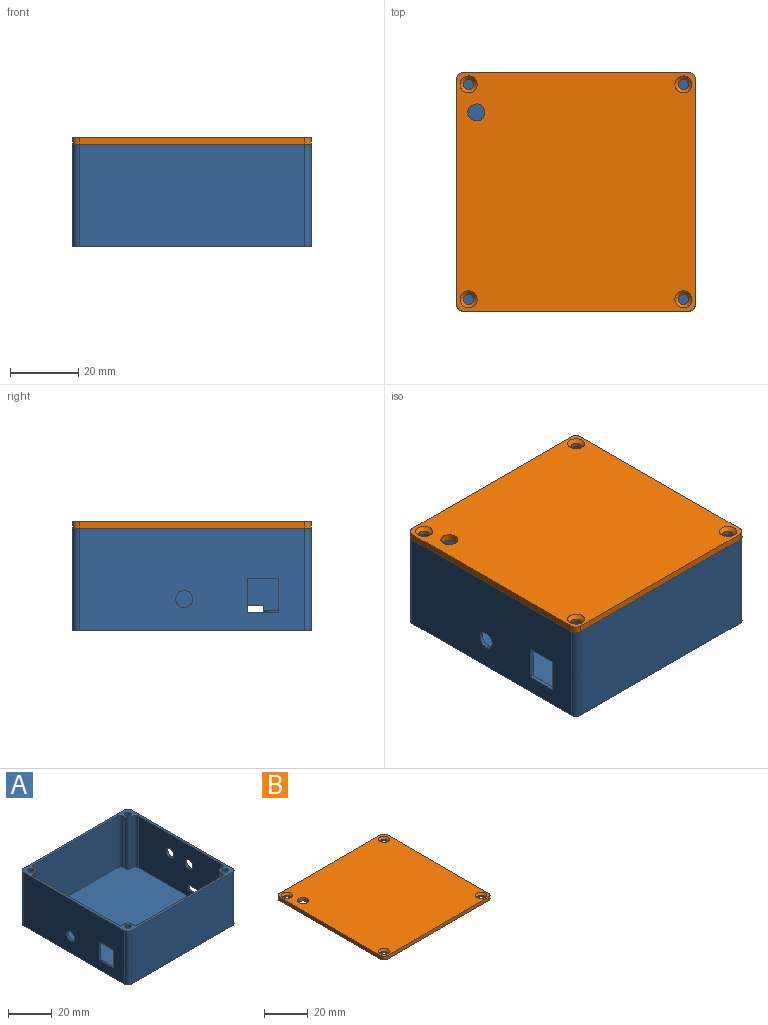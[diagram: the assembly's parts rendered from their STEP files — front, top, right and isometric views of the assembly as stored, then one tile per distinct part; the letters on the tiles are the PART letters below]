
ASSEMBLY  parts=2 mates=1
PART A: 60 faces, bbox 70x70x30 mm
  f0: plane 54x29mm, normal (1,0,0), area 1454.2mm2, adj f4,f7,f43,f48,f55,f56,f57,f58
  f1: plane 66x30mm, normal (-1,0,0), area 1868.2mm2, adj f7,f10,f27,f28,f55,f56,f57,f58
  f2: plane 54x29mm, normal (-1,0,0), area 1478.7mm2, adj f4,f7,f39,f42,f49,f50,f51,f52
  f3: plane 66x30mm, normal (1,0,0), area 1892.7mm2, adj f7,f10,f29,f30,f49,f50,f51,f52
  f4: plane 68x68mm, normal (0,0,1), area 4481.3mm2, adj f0,f2,f5,f6,f11,f12,f13,f14
  f5: plane 54x29mm, normal (0,1,0), area 1566mm2, adj f4,f7,f40,f44
  f6: plane 54x29mm, normal (0,-1,0), area 1566mm2, adj f4,f7,f38,f46
  f7: plane 70x70mm, normal (0,0,1), area 347.7mm2, adj f0,f1,f2,f3,f5,f6,f8,f9
  f8: plane 66x30mm, normal (0,1,0), area 1980mm2, adj f7,f10,f27,f30
  f9: plane 66x30mm, normal (0,-1,0), area 1980mm2, adj f7,f10,f28,f29
  f10: plane 70x70mm, normal (0,0,-1), area 4882.4mm2, adj f1,f3,f8,f9,f27,f28,f29,f30
  f11: plane 29x1mm, normal (0,-1,0), area 29mm2, adj f4,f7,f47,f48
  f12: plane 29x1mm, normal (1,0,0), area 29mm2, adj f4,f7,f46,f47
  f13: plane 29x1mm, normal (0,-1,0), area 29mm2, adj f4,f7,f37,f39
  f14: plane 29x1mm, normal (-1,0,0), area 29mm2, adj f4,f7,f37,f38
  f15: plane 29x1mm, normal (0,1,0), area 29mm2, adj f4,f7,f43,f45
  f16: plane 29x1mm, normal (1,0,0), area 29mm2, adj f4,f7,f44,f45
  f17: plane 29x1mm, normal (0,1,0), area 29mm2, adj f4,f7,f41,f42
  f18: plane 29x1mm, normal (-1,0,0), area 29mm2, adj f4,f7,f40,f41
  f19: cylinder r=1.5mm len=10mm, axis (0,0,1), area 94.2mm2, adj f7,f20
  f20: plane 3x3mm, normal (0,0,1), area 7.1mm2, adj f19
  f21: cylinder r=1.5mm len=10mm, axis (0,0,1), area 94.2mm2, adj f7,f22
  f22: plane 3x3mm, normal (0,0,1), area 7.1mm2, adj f21
  f23: cylinder r=1.5mm len=10mm, axis (0,0,1), area 94.2mm2, adj f7,f24
  f24: plane 3x3mm, normal (0,0,1), area 7.1mm2, adj f23
  f25: cylinder r=1.5mm len=10mm, axis (0,0,1), area 94.2mm2, adj f7,f26
  f26: plane 3x3mm, normal (0,0,1), area 7.1mm2, adj f25
  f27: cylinder r=2mm len=30mm, axis (0,0,1), area 94.2mm2, adj f1,f7,f8,f10
  f28: cylinder r=2mm len=30mm, axis (0,0,-1), area 94.2mm2, adj f1,f7,f9,f10
  f29: cylinder r=2mm len=30mm, axis (0,0,1), area 94.2mm2, adj f3,f7,f9,f10
  f30: cylinder r=2mm len=30mm, axis (0,0,-1), area 94.2mm2, adj f3,f7,f8,f10
  f31: cylinder r=1.5mm len=6mm, axis (0,0,-1), area 56.5mm2, adj f10,f33
  f32: cylinder r=2.5mm len=5mm, axis (0,0,-1), area 78.5mm2, adj f4,f33
  f33: plane 5x5mm, normal (0,0,1), area 12.6mm2, adj f31,f32
  f34: cylinder r=1.5mm len=6mm, axis (0,0,-1), area 56.5mm2, adj f10,f36
  f35: cylinder r=2.5mm len=5mm, axis (0,0,-1), area 78.5mm2, adj f4,f36
  f36: plane 5x5mm, normal (0,0,1), area 12.6mm2, adj f34,f35
  f37: cylinder r=2mm len=29mm, axis (0,0,1), area 91.1mm2, adj f4,f7,f13,f14
  f38: cylinder r=2mm len=29mm, axis (0,0,1), area 91.1mm2, adj f4,f6,f7,f14
  f39: cylinder r=2mm len=29mm, axis (0,0,-1), area 91.1mm2, adj f2,f4,f7,f13
  f40: cylinder r=2mm len=29mm, axis (0,0,1), area 91.1mm2, adj f4,f5,f7,f18
  f41: cylinder r=2mm len=29mm, axis (0,0,1), area 91.1mm2, adj f4,f7,f17,f18
  f42: cylinder r=2mm len=29mm, axis (0,0,1), area 91.1mm2, adj f2,f4,f7,f17
  f43: cylinder r=2mm len=29mm, axis (0,0,1), area 91.1mm2, adj f0,f4,f7,f15
  f44: cylinder r=2mm len=29mm, axis (0,0,-1), area 91.1mm2, adj f4,f5,f7,f16
  f45: cylinder r=2mm len=29mm, axis (0,0,1), area 91.1mm2, adj f4,f7,f15,f16
  f46: cylinder r=2mm len=29mm, axis (0,0,-1), area 91.1mm2, adj f4,f6,f7,f12
  f47: cylinder r=2mm len=29mm, axis (0,0,1), area 91.1mm2, adj f4,f7,f11,f12
  f48: cylinder r=2mm len=29mm, axis (0,0,-1), area 91.1mm2, adj f0,f4,f7,f11
  f49: cylinder r=2.5mm len=5mm, axis (1,0,0), area 15.7mm2, adj f2,f3
  f50: cylinder r=2.5mm len=5mm, axis (1,0,0), area 15.7mm2, adj f2,f3
  f51: plane 16x1mm, normal (0,0,-1), area 16mm2, adj f2,f3,f52,f54
  f52: plane 3x1mm, normal (0,1,0), area 3mm2, adj f2,f3,f51,f53
  f53: plane 16x1mm, normal (0,0,1), area 16mm2, adj f2,f3,f52,f54
  f54: plane 3x1mm, normal (0,-1,0), area 3mm2, adj f2,f3,f51,f53
  f55: plane 9.22x1mm, normal (0,0,-1), area 9.2mm2, adj f0,f1,f56,f58
  f56: plane 10x1mm, normal (0,-1,0), area 10mm2, adj f0,f1,f55,f57
  f57: plane 9.22x1mm, normal (0,0,1), area 9.2mm2, adj f0,f1,f56,f58
  f58: plane 10x1mm, normal (0,1,0), area 10mm2, adj f0,f1,f55,f57
  f59: cylinder r=2.5mm len=5mm, axis (-1,0,0), area 15.7mm2, adj f0,f1
PART B: 19 faces, bbox 70x70x2 mm
  f0: plane 66x2mm, normal (0,1,0), area 132mm2, adj f5,f6,f15,f18
  f1: plane 66x2mm, normal (-1,0,0), area 132mm2, adj f5,f6,f15,f16
  f2: plane 66x2mm, normal (0,-1,0), area 132mm2, adj f5,f6,f16,f17
  f3: cylinder r=2.5mm len=5mm, axis (0,0,-1), area 31.4mm2, adj f5,f6
  f4: plane 66x2mm, normal (1,0,0), area 132mm2, adj f5,f6,f17,f18
  f5: plane 70x70mm, normal (0,0,1), area 4798.4mm2, adj f0,f1,f2,f3,f4,f11,f12,f13
  f6: plane 70x70mm, normal (0,0,-1), area 4848.7mm2, adj f0,f1,f2,f3,f4,f7,f8,f9
  f7: cylinder r=1.5mm len=3mm, axis (0,0,1), area 9.4mm2, adj f6,f12
  f8: cylinder r=1.5mm len=3mm, axis (0,0,1), area 9.4mm2, adj f6,f11
  f9: cylinder r=1.5mm len=3mm, axis (0,0,1), area 9.4mm2, adj f6,f13
  f10: cylinder r=1.5mm len=3mm, axis (0,0,1), area 9.4mm2, adj f6,f14
  f11: cone r=1.5mm half-angle=45deg, axis (0,0,1), area 17.8mm2, adj f5,f8
  f12: cone r=1.5mm half-angle=45deg, axis (0,0,1), area 17.8mm2, adj f5,f7
  f13: cone r=1.5mm half-angle=45deg, axis (0,0,1), area 17.8mm2, adj f5,f9
  f14: cone r=1.5mm half-angle=45deg, axis (0,0,1), area 17.8mm2, adj f5,f10
  f15: cylinder r=2mm len=2mm, axis (0,0,1), area 6.3mm2, adj f0,f1,f5,f6
  f16: cylinder r=2mm len=2mm, axis (0,0,-1), area 6.3mm2, adj f1,f2,f5,f6
  f17: cylinder r=2mm len=2mm, axis (0,0,1), area 6.3mm2, adj f2,f4,f5,f6
  f18: cylinder r=2mm len=2mm, axis (0,0,-1), area 6.3mm2, adj f0,f4,f5,f6
PLACE A at identity fixed
PLACE B t=(-3.02,75.06,30)mm
MATE slider A.f19 <-> B.f7  axis (0,0,1) through (-67.98,10,30)mm
